# Revit family: Platek_Flamingo_Applique2
name_source: partatom
category: Apparecchi per illuminazione
revit_build: Autodesk Revit 2017 (Build: 20160225_1515(x64)
units: mm (PartAtom-declared; Revit-internal decimal feet)

## family parameters
Basato su piano di lavoro = No
Condiviso = No
Punto di calcolo locali = No
Quota connettore circolare = Usa diametro
Sempre verticale = Sì
Sorgente d'illuminazione = Sì
Taglio con vuoti quando caricato = No
Tipo di parte = Normale

## types (2) — shared parameters
Angolo inclinazione = 90.00°
Beam Angle = 76.00°
Body = PLK_Black
CRI = >80
Cable Lenght = 3 (2x1 mm²)
Carico apparente = 0 VA
Colour Temperature = 3000 K
Commenti sul tipo = Facades
Descrizione = Outdoor Lighting, Wall mounted
Diffuse Type = Polycarbonate
Dimmable = No
Emetti da diametro cerchio = 25 mm  [stored 0.082021 ft]
Energy Efficiency Rating = A/A+/A++
Filtro dei colori = 16777215
Frequency = 50/60 Hz
IK Rating = IK 06
IP Rating = IP65
Insulation Class = 1
LED Protection = Surge protection included
Lampada = LED
Light Source = PLK_Light Source
Luminaire Luminous Flux = 385 lm
Luminaire Luminous Intensity = 259 cd
Luminaire Wattage = 9 W
Manufacturer Comment = IP68 connector included
Modello = Flamingo Applique
Mounting Type = Wall
Nota chiave = Other LED colors available on request
Power Supply Unit = Included
Product Documentation Link = http://www.platek.eu
Product Page URL = http://www.platek.eu
Produttore = PLATEK SRL
Rendi la forma visibile nel rendering = No
Supply Voltage = 230 V
Supply Voltage Max = 240 V
Supply Voltage Min = 220 V
URL = www.platek.eu
Variazione temperatura colore lampada con luminosità attenuata = <Nessuno>

## per-type parameters (varying)
| type | Codice assieme | File diagramma fotometrico | H.850.000_2160.000 | Height | Immagine tipo | PLATEK Article Code | Product Dimension |
| 3010316_9W_LED_3000K_H2160mm | 3010316.01(Black); 3010316.09(Bronze) | 3010316.IES | No | 2160 mm  [stored 7.08661 ft] | flamingo_applique_2.jpg | 3010316 | L1400mm x H850mm |
| 3010216_9W_LED_3000K_H850mm | 3010216.01(Black); 3010216.09(Bronze) | 3010216.IES | Sì | 850 mm  [stored 2.78871 ft] | flamingo_applique_850.jpg | 3010216 | L1.400m x H0.500m |

note: [stored X ft] marks values corroborated as IEEE doubles in the binary element streams (Revit-internal decimal feet)
